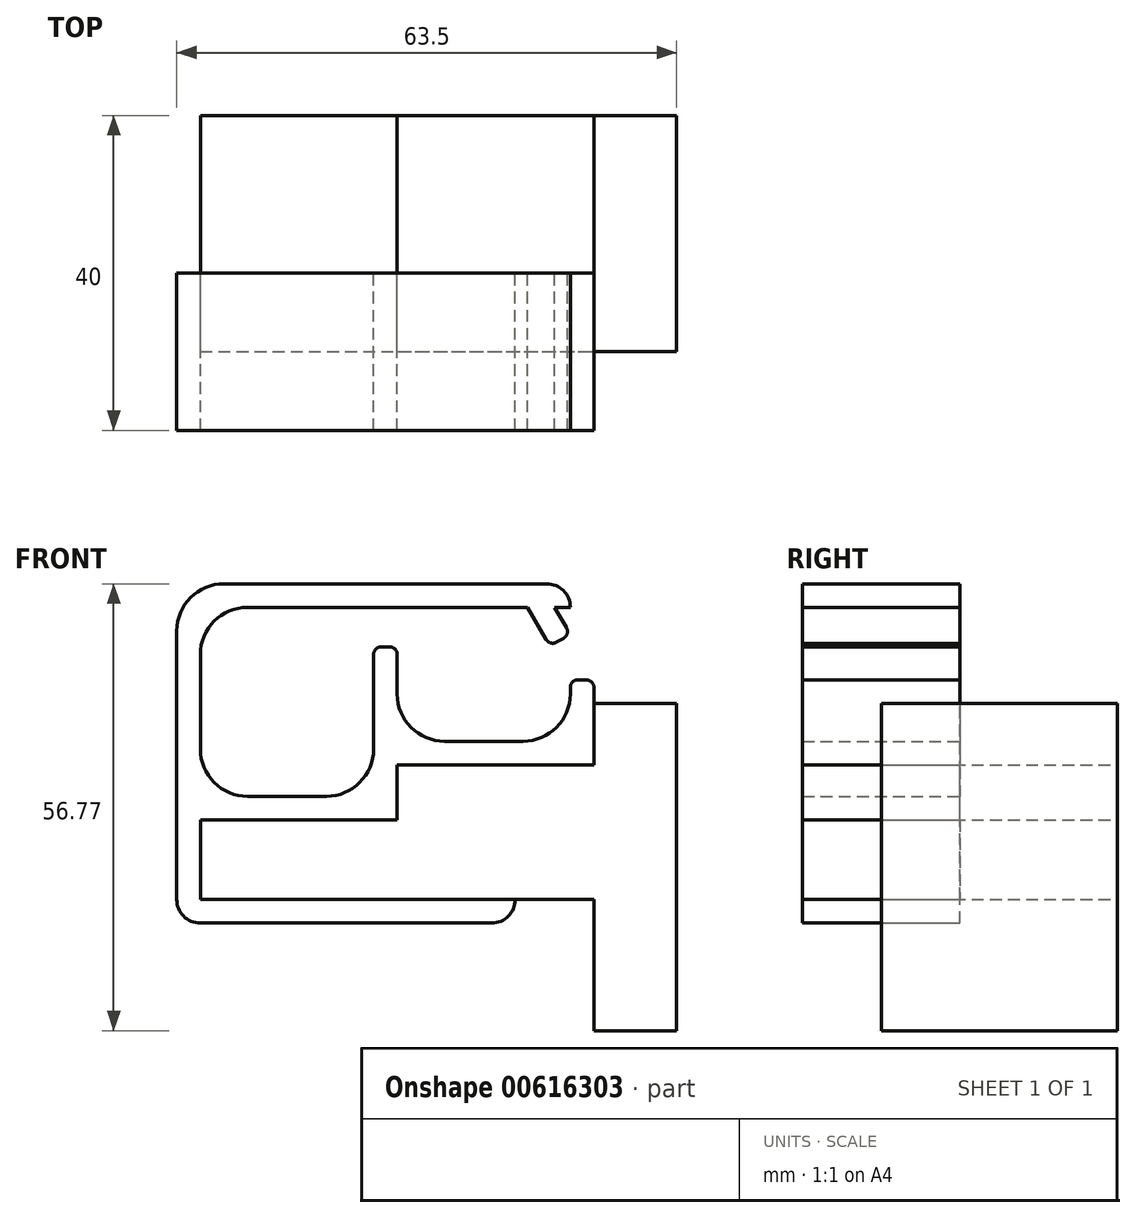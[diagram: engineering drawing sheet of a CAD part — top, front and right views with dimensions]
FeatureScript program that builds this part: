
annotation { "Feature Type Name" : "Feature", "Feature Type Description" : "" }
export const myFeature = defineFeature(function(context is Context, id is Id, definition is map)
    precondition{}
    {
        {
            var Q0;
            Q0=qCreatedBy(makeId("Front.planeOp"),FACE);
            var sketch = newSketch(context, id + "F0", { "sketchPlane" : qUnion([Q0])});
            skLineSegment(sketch, "E0.bottom", {"start": v(-30.5, 5.1) * mm, "end": v(30, 5.1) * mm});
            skLineSegment(sketch, "E0.top", {"start": v(-30.5, -5) * mm, "end": v(30, -5) * mm});
            skLineSegment(sketch, "E0.left", {"start": v(-30.5, 5.1) * mm, "end": v(-30.5, -5) * mm});
            skPoint(sketch, "E0.middle", {"position": v(0, 0) * mm});
            skLineSegment(sketch, "E1.bottom", {"start": v(-5.5, 5.1) * mm, "end": v(30, 5.1) * mm});
            skLineSegment(sketch, "E1.top", {"start": v(-5.5, 12.1) * mm, "end": v(30, 12.1) * mm});
            skLineSegment(sketch, "E1.left", {"start": v(-5.5, 5.1) * mm, "end": v(-5.5, 12.1) * mm});
            skLineSegment(sketch, "E2", {"start": v(19.5, 5.1) * mm, "end": v(19.5, 12.1) * mm});
            skLineSegment(sketch, "E3", {"start": v(30, -5) * mm, "end": v(30, 19.9) * mm});
            skLineSegment(sketch, "E4", {"start": v(30, 19.9) * mm, "end": v(19.5, 19.9) * mm});
            skLineSegment(sketch, "E5", {"start": v(19.5, 19.9) * mm, "end": v(19.5, -5) * mm});
            skLineSegment(sketch, "E6.bottom", {"start": v(19.5, -5) * mm, "end": v(30, -5) * mm});
            skLineSegment(sketch, "E6.top", {"start": v(19.5, -21.67) * mm, "end": v(30, -21.67) * mm});
            skLineSegment(sketch, "E6.left", {"start": v(19.5, -5) * mm, "end": v(19.5, -21.67) * mm});
            skLineSegment(sketch, "E6.right", {"start": v(30, -5) * mm, "end": v(30, -21.67) * mm});
            skSolve(sketch);
        }
        {
            var Q0;
            Q0 = qSketchRegion(id + "F0", true);
            extrude(context, id + "F1", {"entities" : qUnion([Q0]), "depth" : 15 * mm, "offsetDistance" : 25 * mm, "hasSecondDirection" : true, "secondDirectionOppositeDirection" : true, "secondDirectionDepth" : 15 * mm});
        }
        {
            var Q0;
            Q0=makeQuery(id+"F1.opExtrude","CAP_FACE",FACE,{"disambiguationData":[OSD([sQuery(id+"F0.wireOp",EDGE,"E0.bottom"),sQuery(id+"F0.wireOp",EDGE,"E0.top"),sQuery(id+"F0.wireOp",EDGE,"E0.left"),sQuery(id+"F0.wireOp",EDGE,"E1.top"),sQuery(id+"F0.wireOp",EDGE,"E1.left"),sQuery(id+"F0.wireOp",EDGE,"E3"),sQuery(id+"F0.wireOp",EDGE,"E4"),sQuery(id+"F0.wireOp",EDGE,"E5")])],"isStart":false});
            var sketch = newSketch(context, id + "F2", { "sketchPlane" : qUnion([Q0])});
            skLineSegment(sketch, "E7.0", {"start": v(-30.5, 5.1) * mm, "end": v(-5.5, 5.1) * mm});
            skLineSegment(sketch, "E8.0", {"start": v(-30.5, 5.1) * mm, "end": v(-30.5, -5) * mm});
            skLineSegment(sketch, "E9.0", {"start": v(-5.5, 5.1) * mm, "end": v(-5.5, 12.1) * mm});
            skLineSegment(sketch, "E10.0", {"start": v(-5.5, 12.1) * mm, "end": v(19.5, 12.1) * mm});
            skLineSegment(sketch, "E11.0", {"start": v(19.5, 19.9) * mm, "end": v(19.5, 12.1) * mm});
            skLineSegment(sketch, "E12.0", {"start": v(-33.5, 8.1) * mm, "end": v(-33.5, -5) * mm});
            skLineSegment(sketch, "E12.1", {"start": v(-30.5, 8.1) * mm, "end": v(-8.5, 8.1) * mm});
            skLineSegment(sketch, "E12.2", {"start": v(19.5, 22.9) * mm, "end": v(16.5, 22.9) * mm});
            skLineSegment(sketch, "E12.3", {"start": v(16.5, 22.9) * mm, "end": v(16.5, 15.1) * mm});
            skLineSegment(sketch, "E12.4", {"start": v(-5.5, 15.1) * mm, "end": v(16.5, 15.1) * mm});
            skLineSegment(sketch, "E12.5", {"start": v(-8.5, 8.1) * mm, "end": v(-8.5, 15.1) * mm});
            skLineSegment(sketch, "E13.0", {"start": v(-30.5, -5) * mm, "end": v(9.5, -5) * mm});
            skLineSegment(sketch, "E14.0", {"start": v(32.5, -8) * mm, "end": v(32.5, 15) * mm, "construction": true});
            skLineSegment(sketch, "E14.1", {"start": v(-30.5, -8) * mm, "end": v(32.5, -8) * mm, "construction": true});
            skLineSegment(sketch, "E15", {"start": v(-33.5, -5) * mm, "end": v(-33.5, -8) * mm});
            skLineSegment(sketch, "E16", {"start": v(-33.5, -8) * mm, "end": v(9.5, -8) * mm});
            skLineSegment(sketch, "E17", {"start": v(9.5, -8) * mm, "end": v(9.5, -5) * mm});
            skLineSegment(sketch, "E18", {"start": v(9.5, -5) * mm, "end": v(-30.5, -5) * mm});
            skLineSegment(sketch, "E19", {"start": v(19.5, 19.9) * mm, "end": v(30, 19.9) * mm});
            skPoint(sketch, "E20.0.start.orphan", {"position": v(-30.5, -5) * mm});
            skLineSegment(sketch, "E21", {"start": v(-33.5, 8.1) * mm, "end": v(-33.5, 35.1) * mm});
            skLineSegment(sketch, "E22", {"start": v(-33.5, 35.1) * mm, "end": v(1.83, 35.1) * mm});
            skLineSegment(sketch, "E23.0", {"start": v(-30.5, 32.1) * mm, "end": v(11.04, 32.1) * mm});
            skLineSegment(sketch, "E23.1", {"start": v(-30.5, 8.1) * mm, "end": v(-30.5, 32.1) * mm});
            skLineSegment(sketch, "E24", {"start": v(11.04, 32.1) * mm, "end": v(16.5, 32.1) * mm});
            skLineSegment(sketch, "E25", {"start": v(16.5, 32.1) * mm, "end": v(16.5, 35.1) * mm});
            skLineSegment(sketch, "E26", {"start": v(16.5, 35.1) * mm, "end": v(1.83, 35.1) * mm});
            skLineSegment(sketch, "E27", {"start": v(11.04, 32.1) * mm, "end": v(13.9, 27.18) * mm});
            skLineSegment(sketch, "E28", {"start": v(13.9, 27.18) * mm, "end": v(16.5, 28.68) * mm});
            skLineSegment(sketch, "E29", {"start": v(16.5, 28.68) * mm, "end": v(12.76, 35.1) * mm});
            skLineSegment(sketch, "E30", {"start": v(-5.5, 12.1) * mm, "end": v(-5.5, 27.1) * mm});
            skLineSegment(sketch, "E31", {"start": v(-5.5, 27.1) * mm, "end": v(-8.5, 27.1) * mm});
            skLineSegment(sketch, "E32", {"start": v(-8.5, 27.1) * mm, "end": v(-8.5, 15.1) * mm});
            skLineSegment(sketch, "E33", {"start": v(19.5, 19.9) * mm, "end": v(19.5, 22.9) * mm});
            skSolve(sketch);
        }
        {
            var Q0;
            Q0 = qSketchRegion(id + "F2", true);
            extrude(context, id + "F3", {"entities" : qUnion([Q0]), "depth" : 10 * mm, "offsetDistance" : 25 * mm, "hasSecondDirection" : true, "secondDirectionOppositeDirection" : true, "secondDirectionDepth" : 10 * mm});
        }
        {
            var Q0;
            Q0=makeQuery(id+"F3.opExtrude","SWEPT_EDGE",EDGE,{"disambiguationData":[OSD([sQuery(id+"F2.wireOp",EDGE,"E12.1"),sQuery(id+"F2.wireOp",EDGE,"E23.1")])]});
            var Q1;
            Q1=makeQuery(id+"F3.opExtrude","SWEPT_EDGE",EDGE,{"disambiguationData":[OSD([sQuery(id+"F2.wireOp",EDGE,"E23.0"),sQuery(id+"F2.wireOp",EDGE,"E23.1")])]});
            var Q2;
            Q2=makeQuery(id+"F3.opExtrude","SWEPT_EDGE",EDGE,{"disambiguationData":[OSD([sQuery(id+"F2.wireOp",EDGE,"E12.1"),sQuery(id+"F2.wireOp",EDGE,"E12.5")])]});
            var Q3;
            Q3=makeQuery(id+"F3.opExtrude","SWEPT_EDGE",EDGE,{"disambiguationData":[OSD([sQuery(id+"F2.wireOp",EDGE,"E12.3"),sQuery(id+"F2.wireOp",EDGE,"E12.4")])]});
            var Q4;
            Q4=makeQuery(id+"F3.opExtrude","SWEPT_EDGE",EDGE,{"disambiguationData":[OSD([sQuery(id+"F2.wireOp",EDGE,"E21"),sQuery(id+"F2.wireOp",EDGE,"E22")])]});
            var Q5;
            Q5=makeQuery(id+"F3.opExtrude","SWEPT_EDGE",EDGE,{"disambiguationData":[OSD([sQuery(id+"F2.wireOp",EDGE,"E12.4"),sQuery(id+"F2.wireOp",EDGE,"E30")])]});
            fillet(context, id + "F4", {"entities" : qUnion([Q0, Q1, Q2, Q3, Q4, Q5]), "radius" : 6 * mm, "tangentPropagation" : true, "allowEdgeOverflow" : false});
        }
        {
            var Q0;
            Q0=makeQuery(id+"F3.opExtrude","SWEPT_EDGE",EDGE,{"disambiguationData":[OSD([sQuery(id+"F2.wireOp",EDGE,"E15"),sQuery(id+"F2.wireOp",EDGE,"E16")])]});
            var Q1;
            Q1=makeQuery(id+"F3.opExtrude","SWEPT_EDGE",EDGE,{"disambiguationData":[OSD([sQuery(id+"F2.wireOp",EDGE,"E16"),sQuery(id+"F2.wireOp",EDGE,"E17")])]});
            var Q2;
            Q2=makeQuery(id+"F3.opExtrude","SWEPT_EDGE",EDGE,{"disambiguationData":[OSD([sQuery(id+"F2.wireOp",EDGE,"E25"),sQuery(id+"F2.wireOp",EDGE,"E26")])]});
            fillet(context, id + "F5", {"entities" : qUnion([Q0, Q1, Q2]), "radius" : 3 * mm, "tangentPropagation" : true, "allowEdgeOverflow" : false});
        }
        {
            var Q0;
            Q0=makeQuery(id+"F3.opExtrude","SWEPT_EDGE",EDGE,{"disambiguationData":[OSD([sQuery(id+"F2.wireOp",EDGE,"E27"),sQuery(id+"F2.wireOp",EDGE,"E28")])]});
            var Q1;
            Q1=makeQuery(id+"F3.opExtrude","SWEPT_EDGE",EDGE,{"disambiguationData":[OSD([sQuery(id+"F2.wireOp",EDGE,"E28"),sQuery(id+"F2.wireOp",EDGE,"E29")])]});
            var Q2;
            Q2=makeQuery(id+"F3.opExtrude","SWEPT_EDGE",EDGE,{"disambiguationData":[OSD([sQuery(id+"F2.wireOp",EDGE,"E31"),sQuery(id+"F2.wireOp",EDGE,"E32")])]});
            var Q3;
            Q3=makeQuery(id+"F3.opExtrude","SWEPT_EDGE",EDGE,{"disambiguationData":[OSD([sQuery(id+"F2.wireOp",EDGE,"E30"),sQuery(id+"F2.wireOp",EDGE,"E31")])]});
            var Q4;
            Q4=makeQuery(id+"F3.opExtrude","SWEPT_EDGE",EDGE,{"disambiguationData":[OSD([sQuery(id+"F2.wireOp",EDGE,"E12.2"),sQuery(id+"F2.wireOp",EDGE,"vB52ZnIE-sQYg-arS7-V4vk-xVdBZ2ELF7Tn")])]});
            var Q5;
            Q5=makeQuery(id+"F3.opExtrude","SWEPT_EDGE",EDGE,{"disambiguationData":[OSD([sQuery(id+"F2.wireOp",EDGE,"E12.2"),sQuery(id+"F2.wireOp",EDGE,"E12.3")])]});
            fillet(context, id + "F6", {"entities" : qUnion([Q0, Q1, Q2, Q3, Q4, Q5]), "radius" : 1 * mm, "tangentPropagation" : true, "allowEdgeOverflow" : false});
        }
    });
